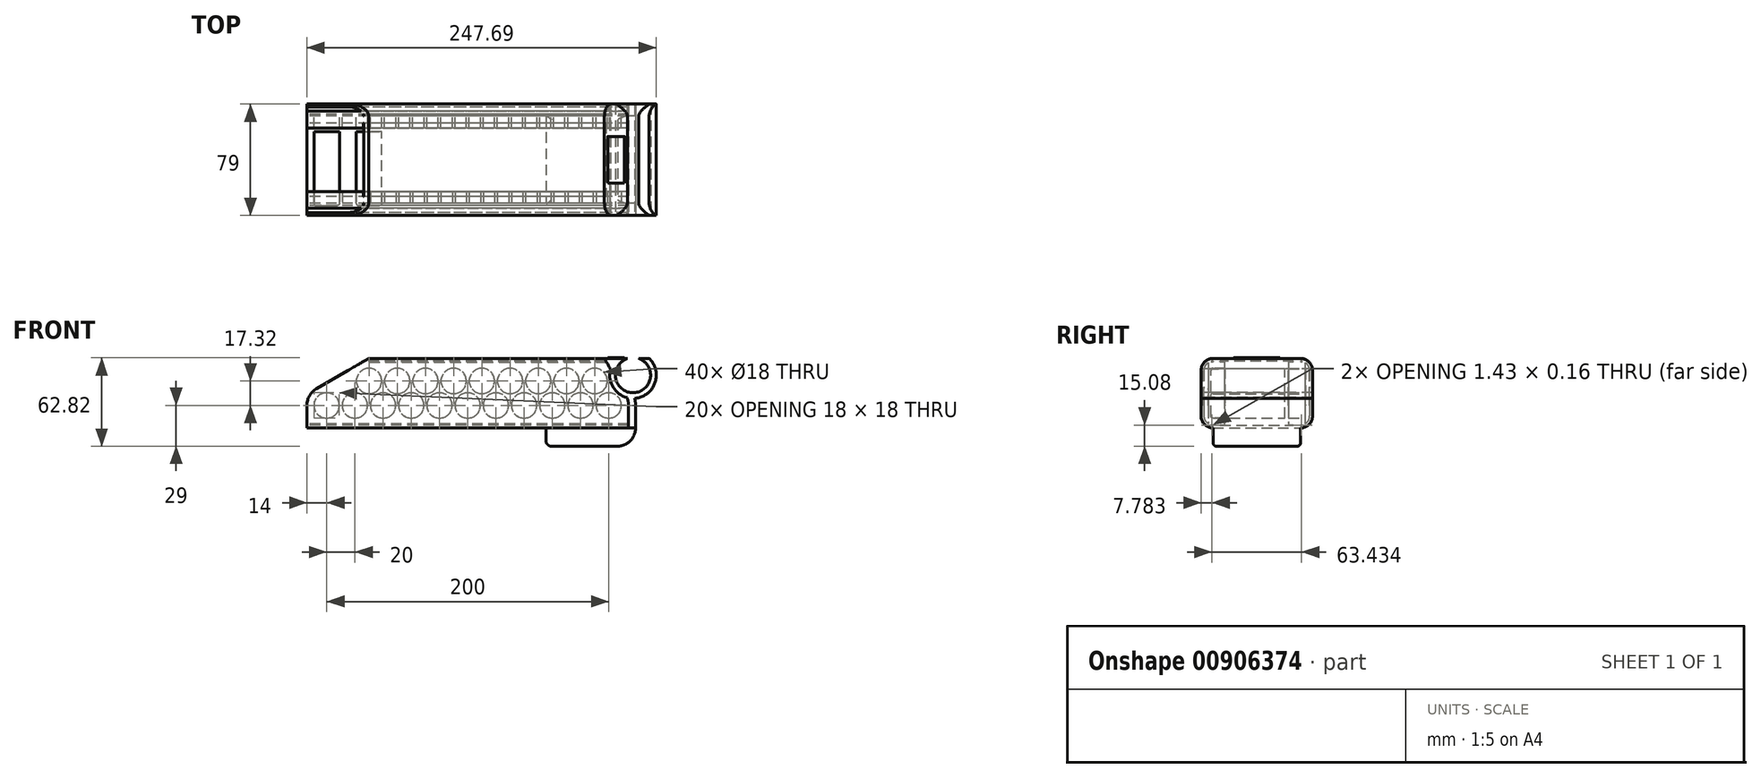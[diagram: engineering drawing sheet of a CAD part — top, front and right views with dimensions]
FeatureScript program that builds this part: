
annotation { "Feature Type Name" : "Feature", "Feature Type Description" : "" }
export const myFeature = defineFeature(function(context is Context, id is Id, definition is map)
    precondition{}
    {
        {
            var Q0;
            Q0=qCreatedBy(makeId("Front.planeOp"),FACE);
            var sketch = newSketch(context, id + "F0", { "sketchPlane" : qUnion([Q0])});
            skCircle(sketch, "E0", {"center": v(0, 0) * mm, "radius": 9 * mm});
            skCircle(sketch, "E1.0.1.0", {"center": v(30, 17.32) * mm, "radius": 9 * mm});
            skCircle(sketch, "E1.1.0.0", {"center": v(20, 0) * mm, "radius": 9 * mm});
            skCircle(sketch, "E1.1.1.0", {"center": v(50, 17.32) * mm, "radius": 9 * mm});
            skCircle(sketch, "E1.2.0.0", {"center": v(40, 0) * mm, "radius": 9 * mm});
            skCircle(sketch, "E1.2.1.0", {"center": v(70, 17.32) * mm, "radius": 9 * mm});
            skCircle(sketch, "E1.3.0.0", {"center": v(60, 0) * mm, "radius": 9 * mm});
            skCircle(sketch, "E1.3.1.0", {"center": v(90, 17.32) * mm, "radius": 9 * mm});
            skCircle(sketch, "E1.4.0.0", {"center": v(80, 0) * mm, "radius": 9 * mm});
            skCircle(sketch, "E1.4.1.0", {"center": v(110, 17.32) * mm, "radius": 9 * mm});
            skCircle(sketch, "E1.5.0.0", {"center": v(100, 0) * mm, "radius": 9 * mm});
            skCircle(sketch, "E1.5.1.0", {"center": v(130, 17.32) * mm, "radius": 9 * mm});
            skCircle(sketch, "E1.6.0.0", {"center": v(120, 0) * mm, "radius": 9 * mm});
            skCircle(sketch, "E1.6.1.0", {"center": v(150, 17.32) * mm, "radius": 9 * mm});
            skCircle(sketch, "E1.7.0.0", {"center": v(140, 0) * mm, "radius": 9 * mm});
            skCircle(sketch, "E1.7.1.0", {"center": v(170, 17.32) * mm, "radius": 9 * mm});
            skCircle(sketch, "E1.8.0.0", {"center": v(160, 0) * mm, "radius": 9 * mm});
            skCircle(sketch, "E1.8.1.0", {"center": v(190, 17.32) * mm, "radius": 9 * mm});
            skCircle(sketch, "E1.9.0.0", {"center": v(180, 0) * mm, "radius": 9 * mm});
            skLineSegment(sketch, "E1.direction1", {"start": v(0, 0) * mm, "end": v(20, 0) * mm, "construction": true});
            skLineSegment(sketch, "E1.direction2", {"start": v(0, 0) * mm, "end": v(30, 17.32) * mm, "construction": true});
            skCircle(sketch, "E2.0.10.0", {"center": v(200, 0) * mm, "radius": 9 * mm});
            skCircle(sketch, "E3", {"center": v(217.19, 21.47) * mm, "radius": 16.5 * mm});
            skCircle(sketch, "E4", {"center": v(217.19, 21.47) * mm, "radius": 12.5 * mm});
            skSolve(sketch);
        }
        {
            var Q0;
            Q0=makeQuery(id+"F0.imprint","IMPRINT",FACE,{"disambiguationData":[TD([[makeQuery(id+"F0.imprint","IMPRINT",EDGE,{"derivedFrom":sQuery(id+"F0.wireOp",EDGE,"E0")}),1.0]])]});
            var Q1;
            Q1=makeQuery(id+"F0.imprint","IMPRINT",FACE,{"disambiguationData":[TD([[makeQuery(id+"F0.imprint","IMPRINT",EDGE,{"derivedFrom":sQuery(id+"F0.wireOp",EDGE,"E1.0.1.0")}),1.0]])]});
            extrude(context, id + "F1", {"entities" : qUnion([Q0, Q1]), "depth" : 65 * mm, "offsetDistance" : 25 * mm});
        }
        {
            var Q0;
            Q0=makeQuery(id+"F1.opExtrude","CAP_FACE",FACE,{"disambiguationData":[OSD([sQuery(id+"F0.wireOp",EDGE,"E1.0.1.0")])],"isStart":false});
            var Q1;
            Q1=makeQuery(id+"F1.opExtrude","CAP_FACE",FACE,{"disambiguationData":[OSD([sQuery(id+"F0.wireOp",EDGE,"E0")])],"isStart":false});
            var Q2;
            Q2=makeQuery(id+"F1.opExtrude","CAP_FACE",FACE,{"disambiguationData":[OSD([sQuery(id+"F0.wireOp",EDGE,"E0")])],"isStart":true});
            var Q3;
            Q3=makeQuery(id+"F1.opExtrude","CAP_FACE",FACE,{"disambiguationData":[OSD([sQuery(id+"F0.wireOp",EDGE,"E1.0.1.0")])],"isStart":true});
            fillet(context, id + "F2", {"entities" : qUnion([Q0, Q1, Q2, Q3]), "radius" : 1.5 * mm, "tangentPropagation" : true, "allowEdgeOverflow" : false});
        }
        {
            var Q0;
            Q0=qCreatedBy(makeId("Right.planeOp"),FACE);
            cPlane(context, id + "F3", {"entities" : qUnion([Q0]), "cplaneType" : CPlaneType.OFFSET, "offset" : 50 * mm, "oppositeDirection" : true, "width" : 150 * mm, "height" : 150 * mm});
        }
        {
            var Q0;
            Q0=qCreatedBy(id+"F3.planeOp",FACE);
            var sketch = newSketch(context, id + "F4", { "sketchPlane" : qUnion([Q0])});
            skLineSegment(sketch, "E5", {"start": v(-10, 31.16) * mm, "end": v(-6.5, 31.16) * mm});
            skLineSegment(sketch, "E6", {"start": v(-1.5, 31.16) * mm, "end": v(-1.5, 30.16) * mm});
            skLineSegment(sketch, "E7", {"start": v(-1.5, 30.16) * mm, "end": v(-6.5, 30.16) * mm});
            skLineSegment(sketch, "E8", {"start": v(-6.5, 30.16) * mm, "end": v(-6.5, 31.16) * mm});
            skLineSegment(sketch, "E9.trimOffspring", {"start": v(-1.5, 31.16) * mm, "end": v(2, 31.16) * mm});
            skPoint(sketch, "E10", {"position": v(-1.5, -9) * mm});
            skPoint(sketch, "E11", {"position": v(-1.5, 26.32) * mm});
            skLineSegment(sketch, "E12", {"start": v(-1.5, 26.32) * mm, "end": v(-1.5, -9) * mm, "construction": true});
            skLineSegment(sketch, "E13", {"start": v(-1.5, 8.66) * mm, "end": v(15.76, 8.66) * mm, "construction": true});
            skLineSegment(sketch, "E14", {"start": v(2, 31.16) * mm, "end": v(2, 8.66) * mm});
            skLineSegment(sketch, "E15", {"start": v(-10, 31.16) * mm, "end": v(-10, 8.66) * mm});
            skLineSegment(sketch, "E16.MirrorCS", {"start": v(2, -13.84) * mm, "end": v(2, 8.66) * mm});
            skLineSegment(sketch, "E17.MirrorCS", {"start": v(-1.5, -13.84) * mm, "end": v(2, -13.84) * mm});
            skLineSegment(sketch, "E18.MirrorCS", {"start": v(-1.5, -13.84) * mm, "end": v(-1.5, -12.84) * mm});
            skLineSegment(sketch, "E19.MirrorCS", {"start": v(-1.5, -12.84) * mm, "end": v(-6.5, -12.84) * mm});
            skLineSegment(sketch, "E20.MirrorCS", {"start": v(-10, -13.84) * mm, "end": v(-6.5, -13.84) * mm});
            skLineSegment(sketch, "E21.MirrorCS", {"start": v(-10, -13.84) * mm, "end": v(-10, 8.66) * mm});
            skLineSegment(sketch, "E22.MirrorCS", {"start": v(-6.5, -12.84) * mm, "end": v(-6.5, -13.84) * mm});
            skSolve(sketch);
        }
        {
            var Q0;
            Q0=makeQuery(id+"F4.imprint","IMPRINT",FACE,{"disambiguationData":[TD([[makeQuery(id+"F4.imprint","IMPRINT",EDGE,{"derivedFrom":sQuery(id+"F4.wireOp",EDGE,"E5")}),-1.0]])]});
            extrude(context, id + "F5", {"entities" : qUnion([Q0]), "depth" : 300 * mm, "offsetDistance" : 25 * mm});
        }
        {
            var Q0;
            Q0=makeQuery(id+"F0.imprint","IMPRINT",FACE,{"disambiguationData":[TD([[makeQuery(id+"F0.imprint","IMPRINT",EDGE,{"derivedFrom":sQuery(id+"F0.wireOp",EDGE,"E1.1.0.0")}),1.0]])]});
            var Q1;
            Q1=makeQuery(id+"F0.imprint","IMPRINT",FACE,{"disambiguationData":[TD([[makeQuery(id+"F0.imprint","IMPRINT",EDGE,{"derivedFrom":sQuery(id+"F0.wireOp",EDGE,"E1.2.0.0")}),1.0]])]});
            var Q2;
            Q2=makeQuery(id+"F0.imprint","IMPRINT",FACE,{"disambiguationData":[TD([[makeQuery(id+"F0.imprint","IMPRINT",EDGE,{"derivedFrom":sQuery(id+"F0.wireOp",EDGE,"E0")}),1.0]])]});
            var Q3;
            Q3=makeQuery(id+"F0.imprint","IMPRINT",FACE,{"disambiguationData":[TD([[makeQuery(id+"F0.imprint","IMPRINT",EDGE,{"derivedFrom":sQuery(id+"F0.wireOp",EDGE,"E1.3.0.0")}),1.0]])]});
            var Q4;
            Q4=makeQuery(id+"F0.imprint","IMPRINT",FACE,{"disambiguationData":[TD([[makeQuery(id+"F0.imprint","IMPRINT",EDGE,{"derivedFrom":sQuery(id+"F0.wireOp",EDGE,"E1.0.1.0")}),1.0]])]});
            var Q5;
            Q5=makeQuery(id+"F0.imprint","IMPRINT",FACE,{"disambiguationData":[TD([[makeQuery(id+"F0.imprint","IMPRINT",EDGE,{"derivedFrom":sQuery(id+"F0.wireOp",EDGE,"E1.1.1.0")}),1.0]])]});
            var Q6;
            Q6=makeQuery(id+"F0.imprint","IMPRINT",FACE,{"disambiguationData":[TD([[makeQuery(id+"F0.imprint","IMPRINT",EDGE,{"derivedFrom":sQuery(id+"F0.wireOp",EDGE,"E1.4.0.0")}),1.0]])]});
            var Q7;
            Q7=makeQuery(id+"F0.imprint","IMPRINT",FACE,{"disambiguationData":[TD([[makeQuery(id+"F0.imprint","IMPRINT",EDGE,{"derivedFrom":sQuery(id+"F0.wireOp",EDGE,"E1.2.1.0")}),1.0]])]});
            var Q8;
            Q8=makeQuery(id+"F0.imprint","IMPRINT",FACE,{"disambiguationData":[TD([[makeQuery(id+"F0.imprint","IMPRINT",EDGE,{"derivedFrom":sQuery(id+"F0.wireOp",EDGE,"E1.3.1.0")}),1.0]])]});
            var Q9;
            Q9=makeQuery(id+"F0.imprint","IMPRINT",FACE,{"disambiguationData":[TD([[makeQuery(id+"F0.imprint","IMPRINT",EDGE,{"derivedFrom":sQuery(id+"F0.wireOp",EDGE,"E1.5.0.0")}),1.0]])]});
            var Q10;
            Q10=makeQuery(id+"F0.imprint","IMPRINT",FACE,{"disambiguationData":[TD([[makeQuery(id+"F0.imprint","IMPRINT",EDGE,{"derivedFrom":sQuery(id+"F0.wireOp",EDGE,"E1.6.0.0")}),1.0]])]});
            var Q11;
            Q11=makeQuery(id+"F0.imprint","IMPRINT",FACE,{"disambiguationData":[TD([[makeQuery(id+"F0.imprint","IMPRINT",EDGE,{"derivedFrom":sQuery(id+"F0.wireOp",EDGE,"E1.4.1.0")}),1.0]])]});
            var Q12;
            Q12=makeQuery(id+"F0.imprint","IMPRINT",FACE,{"disambiguationData":[TD([[makeQuery(id+"F0.imprint","IMPRINT",EDGE,{"derivedFrom":sQuery(id+"F0.wireOp",EDGE,"E1.5.1.0")}),1.0]])]});
            var Q13;
            Q13=makeQuery(id+"F0.imprint","IMPRINT",FACE,{"disambiguationData":[TD([[makeQuery(id+"F0.imprint","IMPRINT",EDGE,{"derivedFrom":sQuery(id+"F0.wireOp",EDGE,"E1.7.0.0")}),1.0]])]});
            var Q14;
            Q14=makeQuery(id+"F0.imprint","IMPRINT",FACE,{"disambiguationData":[TD([[makeQuery(id+"F0.imprint","IMPRINT",EDGE,{"derivedFrom":sQuery(id+"F0.wireOp",EDGE,"E1.8.0.0")}),1.0]])]});
            var Q15;
            Q15=makeQuery(id+"F0.imprint","IMPRINT",FACE,{"disambiguationData":[TD([[makeQuery(id+"F0.imprint","IMPRINT",EDGE,{"derivedFrom":sQuery(id+"F0.wireOp",EDGE,"E1.6.1.0")}),1.0]])]});
            var Q16;
            Q16=makeQuery(id+"F0.imprint","IMPRINT",FACE,{"disambiguationData":[TD([[makeQuery(id+"F0.imprint","IMPRINT",EDGE,{"derivedFrom":sQuery(id+"F0.wireOp",EDGE,"E1.9.0.0")}),1.0]])]});
            var Q17;
            Q17=makeQuery(id+"F0.imprint","IMPRINT",FACE,{"disambiguationData":[TD([[makeQuery(id+"F0.imprint","IMPRINT",EDGE,{"derivedFrom":sQuery(id+"F0.wireOp",EDGE,"E1.7.1.0")}),1.0]])]});
            var Q18;
            Q18=makeQuery(id+"F0.imprint","IMPRINT",FACE,{"disambiguationData":[TD([[makeQuery(id+"F0.imprint","IMPRINT",EDGE,{"derivedFrom":sQuery(id+"F0.wireOp",EDGE,"E1.8.1.0")}),1.0]])]});
            var Q19;
            Q19=makeQuery(id+"F0.imprint","IMPRINT",FACE,{"disambiguationData":[TD([[makeQuery(id+"F0.imprint","IMPRINT",EDGE,{"derivedFrom":sQuery(id+"F0.wireOp",EDGE,"E2.0.10.0")}),1.0]])]});
            var Q20;
            Q20=makeQuery(id+"F0.imprint","IMPRINT",FACE,{"disambiguationData":[TD([[makeQuery(id+"F0.imprint","IMPRINT",EDGE,{"derivedFrom":sQuery(id+"F0.wireOp",EDGE,"E3")}),1.0]])]});
            var Q21;
            Q21=makeQuery(id+"F0.imprint","IMPRINT",FACE,{"disambiguationData":[TD([[makeQuery(id+"F0.imprint","IMPRINT",EDGE,{"derivedFrom":sQuery(id+"F0.wireOp",EDGE,"E4")}),1.0]])]});
            extrude(context, id + "F6", {"entities" : qUnion([Q0, Q1, Q2, Q3, Q4, Q5, Q6, Q7, Q8, Q9, Q10, Q11, Q12, Q13, Q14, Q15, Q16, Q17, Q18, Q19, Q20, Q21]), "operationType" : NewBodyOperationType.REMOVE, "endBound" : BoundingType.SYMMETRIC, "depth" : 25 * mm, "offsetDistance" : 25 * mm});
        }
        {
            var Q0;
            Q0=qCreatedBy(id+"F3.planeOp",FACE);
            var sketch = newSketch(context, id + "F7", { "sketchPlane" : qUnion([Q0])});
            skLineSegment(sketch, "E23", {"start": v(-63.5, 26.32) * mm, "end": v(-1.5, 26.32) * mm, "construction": true});
            skLineSegment(sketch, "E24", {"start": v(-32.5, 26.32) * mm, "end": v(-32.5, -11.54) * mm, "construction": true});
            skSolve(sketch);
        }
        {
            var Q0;
            Q0=sQuery(id+"F7.wireOp",EDGE,"E24");
            cPlane(context, id + "F8", {"entities" : qUnion([Q0]), "cplaneType" : CPlaneType.LINE_ANGLE, "offset" : 25 * mm, "angle" : 90 * degree, "oppositeDirection" : true, "width" : 150 * mm, "height" : 150 * mm});
        }
        {
            var Q0;
            Q0=makeQuery(id+"F5.opExtrude","SWEPT_BODY",BODY,{"disambiguationData":[OSD([sQuery(id+"F4.wireOp",EDGE,"E5"),sQuery(id+"F4.wireOp",EDGE,"GOfXxzIh-MKl5-G1SW-encv-l2kD2u1HkRPf"),sQuery(id+"F4.wireOp",EDGE,"sGYx79DI-effi-Y8B0-5mYI-4x9WzQ8cECE0"),sQuery(id+"F4.wireOp",EDGE,"E6"),sQuery(id+"F4.wireOp",EDGE,"E7"),sQuery(id+"F4.wireOp",EDGE,"E8"),sQuery(id+"F4.wireOp",EDGE,"0fff8e5c-98d8-4951-b7fa-ebcbf429b71a0.MirrorCS"),sQuery(id+"F4.wireOp",EDGE,"65c761b0-a97f-46e1-aada-6f9c72a2409e0.MirrorCS"),sQuery(id+"F4.wireOp",EDGE,"bcdb5b7b-b14c-4f07-bf46-ef241487993a0.MirrorCS"),sQuery(id+"F4.wireOp",EDGE,"ed0ec1d9-44e6-4145-b46c-43663aba06680.MirrorCS"),sQuery(id+"F4.wireOp",EDGE,"8e070cfc-182b-4a56-90c9-7eab96a44dfa0.MirrorCS"),sQuery(id+"F4.wireOp",EDGE,"c2e0f179-9004-4e7f-aabe-193be18498250.MirrorCS"),sQuery(id+"F4.wireOp",EDGE,"E9.trimOffspring"),sQuery(id+"F4.wireOp",EDGE,"f0e1f967-a197-4513-83c4-94e6494bc166.trimOffspring")])]});
            var Q1;
            Q1=qCreatedBy(id+"F8.planeOp",FACE);
            mirror(context, id + "F9", {"entities" : qUnion([Q0]), "mirrorPlane" : qUnion([Q1])});
        }
        {
            var Q0;
            Q0=qCreatedBy(id+"F3.planeOp",FACE);
            var sketch = newSketch(context, id + "F10", { "sketchPlane" : qUnion([Q0])});
            skArc(sketch, "E25", {"start": v(0, 24.82) * mm, "mid": v(-0.44, 25.88) * mm, "end": v(-1.5, 26.32) * mm});
            skArc(sketch, "E26", {"start": v(-1.5, -9) * mm, "mid": v(-0.44, -8.56) * mm, "end": v(0, -7.5) * mm});
            skArc(sketch, "E27", {"start": v(-63.5, 26.32) * mm, "mid": v(-64.56, 25.88) * mm, "end": v(-65, 24.82) * mm});
            skArc(sketch, "E28", {"start": v(-65, -7.5) * mm, "mid": v(-64.56, -8.56) * mm, "end": v(-63.5, -9) * mm});
            skLineSegment(sketch, "E29", {"start": v(0, 24.82) * mm, "end": v(0, -7.5) * mm});
            skLineSegment(sketch, "E30", {"start": v(-1.5, 26.32) * mm, "end": v(-63.5, 26.32) * mm});
            skLineSegment(sketch, "E31", {"start": v(-65, 24.82) * mm, "end": v(-65, -7.5) * mm});
            skLineSegment(sketch, "E32", {"start": v(-63.5, -9) * mm, "end": v(-1.5, -9) * mm});
            skLineSegment(sketch, "E33.0", {"start": v(-63.5, -14) * mm, "end": v(-1.5, -14) * mm});
            skArc(sketch, "E33.1", {"start": v(-70, -7.5) * mm, "mid": v(-68.1, -12.1) * mm, "end": v(-63.5, -14) * mm});
            skArc(sketch, "E33.2", {"start": v(-1.5, -14) * mm, "mid": v(3.1, -12.1) * mm, "end": v(5, -7.5) * mm});
            skLineSegment(sketch, "E33.3", {"start": v(-70, 24.82) * mm, "end": v(-70, -7.5) * mm});
            skLineSegment(sketch, "E33.4", {"start": v(5, 24.82) * mm, "end": v(5, -7.5) * mm});
            skArc(sketch, "E33.5", {"start": v(5, 24.82) * mm, "mid": v(3.1, 29.42) * mm, "end": v(-1.5, 31.32) * mm});
            skLineSegment(sketch, "E33.6", {"start": v(-1.5, 31.32) * mm, "end": v(-63.5, 31.32) * mm});
            skArc(sketch, "E33.7", {"start": v(-63.5, 31.32) * mm, "mid": v(-68.1, 29.42) * mm, "end": v(-70, 24.82) * mm});
            skArc(sketch, "E34.0", {"start": v(7, 24.82) * mm, "mid": v(4.51, 30.83) * mm, "end": v(-1.5, 33.32) * mm});
            skLineSegment(sketch, "E34.1", {"start": v(7, 24.82) * mm, "end": v(7, -7.5) * mm});
            skLineSegment(sketch, "E34.2", {"start": v(-1.5, 33.32) * mm, "end": v(-63.5, 33.32) * mm});
            skArc(sketch, "E34.3", {"start": v(-1.5, -16) * mm, "mid": v(4.51, -13.51) * mm, "end": v(7, -7.5) * mm});
            skArc(sketch, "E34.4", {"start": v(-63.5, 33.32) * mm, "mid": v(-69.51, 30.83) * mm, "end": v(-72, 24.82) * mm});
            skLineSegment(sketch, "E34.5", {"start": v(-72, 24.82) * mm, "end": v(-72, -7.5) * mm});
            skArc(sketch, "E34.6", {"start": v(-72, -7.5) * mm, "mid": v(-69.51, -13.51) * mm, "end": v(-63.5, -16) * mm});
            skLineSegment(sketch, "E34.7", {"start": v(-63.5, -16) * mm, "end": v(-1.5, -16) * mm});
            skLineSegment(sketch, "E35.0", {"start": v(-1.5, 31.32) * mm, "end": v(-1.5, 30.16) * mm});
            skLineSegment(sketch, "E36.0", {"start": v(-1.5, 30.16) * mm, "end": v(-6.5, 30.16) * mm});
            skLineSegment(sketch, "E37.0", {"start": v(-6.5, 31.16) * mm, "end": v(-6.5, 31.32) * mm});
            skLineSegment(sketch, "E38.0", {"start": v(-58.5, 30.16) * mm, "end": v(-58.5, 31.32) * mm});
            skLineSegment(sketch, "E39.0", {"start": v(-63.5, 30.16) * mm, "end": v(-58.5, 30.16) * mm});
            skLineSegment(sketch, "E40.0", {"start": v(-63.5, 31.32) * mm, "end": v(-63.5, 30.16) * mm});
            skLineSegment(sketch, "E41.0", {"start": v(-58.5, -12.84) * mm, "end": v(-58.5, -14) * mm});
            skLineSegment(sketch, "E42.0", {"start": v(-63.5, -12.84) * mm, "end": v(-58.5, -12.84) * mm});
            skLineSegment(sketch, "E43.0", {"start": v(-63.5, -14) * mm, "end": v(-63.5, -12.84) * mm});
            skLineSegment(sketch, "E44.0", {"start": v(-1.5, -12.84) * mm, "end": v(-6.5, -12.84) * mm});
            skLineSegment(sketch, "E45.0", {"start": v(-1.5, -14) * mm, "end": v(-1.5, -12.84) * mm});
            skLineSegment(sketch, "E46.0", {"start": v(-6.5, -12.84) * mm, "end": v(-6.5, -14) * mm});
            skPoint(sketch, "E47.orphan", {"position": v(-1.5, -13.84) * mm});
            skPoint(sketch, "E48.orphan", {"position": v(-6.5, -13.84) * mm});
            skPoint(sketch, "E49.orphan", {"position": v(-58.5, -13.84) * mm});
            skPoint(sketch, "E50.orphan", {"position": v(-63.5, -13.84) * mm});
            skPoint(sketch, "E51.orphan", {"position": v(-63.5, 31.16) * mm});
            skPoint(sketch, "E52.orphan", {"position": v(-58.5, 31.16) * mm});
            skPoint(sketch, "E53.orphan", {"position": v(-6.5, 30.16) * mm});
            skPoint(sketch, "E54.orphan", {"position": v(-1.5, 31.16) * mm});
            skLineSegment(sketch, "E55.0", {"start": v(-6.5, 30.16) * mm, "end": v(-6.5, 31.16) * mm});
            skSolve(sketch);
        }
        {
            var Q0;
            Q0=makeQuery(id+"F10.imprint","IMPRINT",FACE,{"disambiguationData":[TD([[makeQuery(id+"F10.imprint","IMPRINT",EDGE,{"derivedFrom":sQuery(id+"F10.wireOp",EDGE,"E33.0")}),-1.0]])]});
            extrude(context, id + "F11", {"entities" : qUnion([Q0]), "operationType" : NewBodyOperationType.REMOVE, "depth" : 400 * mm, "offsetDistance" : 25 * mm});
        }
        {
            var Q0;
            Q0=makeQuery(id+"F10.imprint","IMPRINT",FACE,{"disambiguationData":[TD([[makeQuery(id+"F10.imprint","IMPRINT",EDGE,{"derivedFrom":sQuery(id+"F10.wireOp",EDGE,"E33.0")}),-1.0]])]});
            extrude(context, id + "F12", {"entities" : qUnion([Q0]), "depth" : 300 * mm, "offsetDistance" : 25 * mm});
        }
        {
            var Q0;
            Q0=qCreatedBy(makeId("Front.planeOp"),FACE);
            cPlane(context, id + "F13", {"entities" : qUnion([Q0]), "cplaneType" : CPlaneType.OFFSET, "offset" : 200 * mm, "oppositeDirection" : true, "width" : 150 * mm, "height" : 150 * mm});
        }
        {
            var Q0;
            Q0=qCreatedBy(id+"F13.planeOp",FACE);
            var sketch = newSketch(context, id + "F14", { "sketchPlane" : qUnion([Q0])});
            skCircle(sketch, "E56.0", {"center": v(30, 17.32) * mm, "radius": 9 * mm});
            skLineSegment(sketch, "E57.0", {"start": v(51.88, 46.12) * mm, "end": v(-7, 12.12) * mm});
            skLineSegment(sketch, "E58.0", {"start": v(-55, -12.5) * mm, "end": v(-55, 29.82) * mm});
            skLineSegment(sketch, "E58.3", {"start": v(-55, 29.82) * mm, "end": v(23.65, 29.82) * mm});
            skArc(sketch, "E59.0", {"start": v(-7, 12.12) * mm, "mid": v(-12.12, 7) * mm, "end": v(-14, 0) * mm});
            skLineSegment(sketch, "E60", {"start": v(-14, 0) * mm, "end": v(-14, -25.46) * mm});
            skLineSegment(sketch, "E61", {"start": v(238.69, 49.58) * mm, "end": v(269.05, 49.58) * mm});
            skLineSegment(sketch, "E62", {"start": v(269.05, 49.58) * mm, "end": v(269.05, -36.3) * mm});
            skLineSegment(sketch, "E63", {"start": v(269.05, -36.3) * mm, "end": v(214, -36.3) * mm});
            skLineSegment(sketch, "E64", {"start": v(-14, -25.46) * mm, "end": v(-63.45, -25.46) * mm});
            skLineSegment(sketch, "E65", {"start": v(-63.45, -25.46) * mm, "end": v(-63.45, 49.58) * mm});
            skLineSegment(sketch, "E66", {"start": v(-63.45, 49.58) * mm, "end": v(52.56, 49.58) * mm});
            skLineSegment(sketch, "E67", {"start": v(52.56, 49.58) * mm, "end": v(51.88, 46.12) * mm});
            skArc(sketch, "E68.0", {"start": v(201.27, 25.8) * mm, "mid": v(202.9, 13.22) * mm, "end": v(212.98, 5.51) * mm});
            skLineSegment(sketch, "E69.0", {"start": v(195.36, 36.03) * mm, "end": v(201.27, 25.8) * mm});
            skArc(sketch, "E70.trimOffspring", {"start": v(202.6, 13.76) * mm, "mid": v(202.52, 13.77) * mm, "end": v(202.43, 13.79) * mm});
            skLineSegment(sketch, "E71", {"start": v(238.69, 49.58) * mm, "end": v(196.26, 49.58) * mm});
            skLineSegment(sketch, "E72", {"start": v(196.26, 49.58) * mm, "end": v(195.36, 36.03) * mm});
            skLineSegment(sketch, "E73.trimOffspring", {"start": v(-14, -12.5) * mm, "end": v(-55, -12.5) * mm});
            skLineSegment(sketch, "E74", {"start": v(214, 0) * mm, "end": v(214, -36.3) * mm});
            skArc(sketch, "E75.trimOffspring", {"start": v(214, 0) * mm, "mid": v(213.71, 2.83) * mm, "end": v(212.85, 5.55) * mm});
            skSolve(sketch);
        }
        {
            var Q0;
            {var subQ1=sQuery(id+"F10.wireOp",EDGE,"E35.0");Q0=makeQuery(id+"F10.imprint","IMPRINT",FACE,{"disambiguationData":[TD([[makeQuery(id+"F10.imprint","IMPRINT",EDGE,{"derivedFrom":subQ1}),-1.0]])]});}
            var Q1;
            Q1=makeQuery(id+"F10.imprint","IMPRINT",FACE,{"disambiguationData":[TD([[makeQuery(id+"F10.imprint","IMPRINT",EDGE,{"derivedFrom":sQuery(id+"F10.wireOp",EDGE,"E44.0")}),1.0]])]});
            var Q2;
            {var subQ2=sQuery(id+"F10.wireOp",EDGE,"E41.0");Q2=makeQuery(id+"F10.imprint","IMPRINT",FACE,{"disambiguationData":[TD([[makeQuery(id+"F10.imprint","IMPRINT",EDGE,{"derivedFrom":subQ2}),-1.0]])]});}
            var Q3;
            {var subQ2=sQuery(id+"F10.wireOp",EDGE,"E38.0");Q3=makeQuery(id+"F10.imprint","IMPRINT",FACE,{"disambiguationData":[TD([[makeQuery(id+"F10.imprint","IMPRINT",EDGE,{"derivedFrom":subQ2}),1.0]])]});}
            extrude(context, id + "F15", {"entities" : qUnion([Q0, Q1, Q2, Q3]), "operationType" : NewBodyOperationType.ADD, "depth" : 300 * mm, "offsetDistance" : 25 * mm, "hasSecondDirection" : true, "secondDirectionOppositeDirection" : false, "secondDirectionDepth" : 25 * mm});
        }
        {
            var Q0;
            {var subQ1=sQuery(id+"F14.wireOp",EDGE,"E58.2");Q0=makeQuery(id+"F14.imprint","IMPRINT",FACE,{"disambiguationData":[TD([[makeQuery(id+"F14.imprint","IMPRINT",EDGE,{"derivedFrom":subQ1}),1.0]])]});}
            var Q1;
            {var subQ4=sQuery(id+"F14.wireOp",EDGE,"4b1b3b87-2225-404d-8d70-db46605fedfe.0");Q1=makeQuery(id+"F14.imprint","IMPRINT",FACE,{"disambiguationData":[TD([[makeQuery(id+"F14.imprint","IMPRINT",EDGE,{"derivedFrom":subQ4}),-1.0]])]});}
            var Q2;
            {var subQ1=sQuery(id+"F14.wireOp",EDGE,"E58.0");Q2=makeQuery(id+"F14.imprint","IMPRINT",FACE,{"disambiguationData":[TD([[makeQuery(id+"F14.imprint","IMPRINT",EDGE,{"derivedFrom":subQ1}),-1.0]])]});}
            var Q3;
            {var subQ1=sQuery(id+"F14.wireOp",EDGE,"E58.0");Q3=makeQuery(id+"F14.imprint","IMPRINT",FACE,{"disambiguationData":[TD([[makeQuery(id+"F14.imprint","IMPRINT",EDGE,{"derivedFrom":subQ1}),1.0]])]});}
            var Q4;
            {var subQ0=sQuery(id+"F14.wireOp",EDGE,"E68.0");var subQ1=sQuery(id+"F14.wireOp",EDGE,"E58.3");var subQ2=makeQuery(id+"F14.imprint","INTERSECT",VERTEX,{"disambiguationData":[OD(0.0)],"derivedFrom":[subQ1,subQ0]});Q4=makeQuery(id+"F14.imprint","IMPRINT",FACE,{"disambiguationData":[TD([[makeQuery(id+"F14.imprint","IMPRINT",EDGE,{"disambiguationData":[TD([[subQ2,-1.0]])],"derivedFrom":subQ1}),-1.0]])]});}
            var Q5;
            {var subQ0=sQuery(id+"F14.wireOp",EDGE,"E68.0");var subQ1=sQuery(id+"F14.wireOp",EDGE,"E58.3");var subQ2=makeQuery(id+"F14.imprint","INTERSECT",VERTEX,{"disambiguationData":[OD(0.0)],"derivedFrom":[subQ1,subQ0]});Q5=makeQuery(id+"F14.imprint","IMPRINT",FACE,{"disambiguationData":[TD([[makeQuery(id+"F14.imprint","IMPRINT",EDGE,{"disambiguationData":[TD([[subQ2,-1.0]])],"derivedFrom":subQ1}),1.0]])]});}
            var Q6;
            Q6=makeQuery(id+"F14.imprint","IMPRINT",FACE,{"disambiguationData":[TD([[makeQuery(id+"F14.imprint","IMPRINT",EDGE,{"derivedFrom":sQuery(id+"F14.wireOp",EDGE,"E61")}),-1.0]])]});
            extrude(context, id + "F16", {"entities" : qUnion([Q0, Q1, Q2, Q3, Q4, Q5, Q6]), "operationType" : NewBodyOperationType.REMOVE, "depth" : 300 * mm, "offsetDistance" : 25 * mm});
        }
        {
            var Q0;
            Q0=makeQuery(id+"F12.opExtrude","SWEPT_FACE",FACE,{"disambiguationData":[OSD([sQuery(id+"F10.wireOp",EDGE,"E34.5")])]});
            var sketch = newSketch(context, id + "F17", { "sketchPlane" : qUnion([Q0])});
            skLineSegment(sketch, "E76.0", {"start": v(201.68, -16) * mm, "end": v(155.46, -16) * mm});
            skArc(sketch, "E77.0", {"start": v(218.33, 5) * mm, "mid": v(232.26, 28.19) * mm, "end": v(205.7, 33.32) * mm});
            skCircle(sketch, "E78.0", {"center": v(217.19, 21.47) * mm, "radius": 12.5 * mm});
            skPoint(sketch, "E79.orphan", {"position": v(-14, -16) * mm});
            skPoint(sketch, "E80.0.start.orphan", {"position": v(185.81, -21) * mm});
            skLineSegment(sketch, "E81.0", {"start": v(205.46, -29) * mm, "end": v(159.46, -29) * mm});
            skLineSegment(sketch, "E82", {"start": v(155.46, -25) * mm, "end": v(155.46, -16) * mm});
            skPoint(sketch, "E83.orphan", {"position": v(-7, 12.12) * mm});
            skArc(sketch, "E84.0", {"start": v(219, 0) * mm, "mid": v(218.83, 2.53) * mm, "end": v(218.33, 5) * mm});
            skLineSegment(sketch, "E84.1", {"start": v(219, 0) * mm, "end": v(219, -7.5) * mm});
            skLineSegment(sketch, "E84.2", {"start": v(219, -7.5) * mm, "end": v(219, -15.97) * mm});
            skLineSegment(sketch, "E85.0", {"start": v(214, 0) * mm, "end": v(214, -7.5) * mm});
            skArc(sketch, "E86.0", {"start": v(214, 0) * mm, "mid": v(213.71, 2.83) * mm, "end": v(212.85, 5.55) * mm});
            skLineSegment(sketch, "E87.0", {"start": v(214, -7.5) * mm, "end": v(214, -16) * mm});
            skArc(sketch, "E88.0", {"start": v(201.27, 25.8) * mm, "mid": v(204.43, 11) * mm, "end": v(218.33, 5) * mm});
            skPoint(sketch, "E89.0.end.orphan", {"position": v(15, 24.82) * mm});
            skArc(sketch, "E90.trimOffspring", {"start": v(218.33, 5) * mm, "mid": v(229.94, 31.93) * mm, "end": v(201.27, 25.8) * mm});
            skArc(sketch, "E91", {"start": v(205.46, -29) * mm, "mid": v(215, -25.37) * mm, "end": v(219, -15.97) * mm});
            skPoint(sketch, "E92.visualSharp", {"position": v(155.46, -29) * mm});
            skArc(sketch, "E92.filletArc", {"start": v(155.46, -25) * mm, "mid": v(156.63, -27.83) * mm, "end": v(159.46, -29) * mm});
            skPoint(sketch, "E93.visualSharp", {"position": v(185.81, 38.32) * mm});
            skPoint(sketch, "E94.orphan", {"position": v(196.93, 33.32) * mm});
            skPoint(sketch, "E95.0.end.orphan", {"position": v(29.71, 33.32) * mm});
            skPoint(sketch, "E96.end.orphan", {"position": v(185.81, 33.32) * mm});
            skLineSegment(sketch, "E97.0", {"start": v(196.93, 33.32) * mm, "end": v(201.27, 25.8) * mm});
            skLineSegment(sketch, "E98", {"start": v(196.93, 33.32) * mm, "end": v(205.7, 33.32) * mm});
            skLineSegment(sketch, "E99", {"start": v(214, -16) * mm, "end": v(201.68, -16) * mm});
            skSolve(sketch);
        }
        {
            var Q0;
            Q0=qCreatedBy(id+"F3.planeOp",FACE);
            var sketch = newSketch(context, id + "F18", { "sketchPlane" : qUnion([Q0])});
            skArc(sketch, "E100.0", {"start": v(30.3, 24.82) * mm, "mid": v(20.99, 47.3) * mm, "end": v(-1.5, 56.62) * mm});
            skLineSegment(sketch, "E100.1", {"start": v(-95.3, 0) * mm, "end": v(-95.3, -7.5) * mm});
            skLineSegment(sketch, "E100.2", {"start": v(-95.3, 12.12) * mm, "end": v(-95.3, 0) * mm});
            skLineSegment(sketch, "E100.3", {"start": v(-95.3, 24.82) * mm, "end": v(-95.3, 12.12) * mm});
            skArc(sketch, "E100.4", {"start": v(-63.5, 56.62) * mm, "mid": v(-85.99, 47.3) * mm, "end": v(-95.3, 24.82) * mm});
            skArc(sketch, "E100.5", {"start": v(-95.3, -7.5) * mm, "mid": v(-85.99, -29.99) * mm, "end": v(-63.5, -39.3) * mm});
            skLineSegment(sketch, "E100.6", {"start": v(-1.5, 56.62) * mm, "end": v(-63.5, 56.62) * mm});
            skLineSegment(sketch, "E100.7", {"start": v(-63.5, -39.3) * mm, "end": v(-1.5, -39.3) * mm});
            skArc(sketch, "E100.8", {"start": v(-1.5, -39.3) * mm, "mid": v(20.99, -29.99) * mm, "end": v(30.3, -7.5) * mm});
            skLineSegment(sketch, "E100.9", {"start": v(30.3, 0) * mm, "end": v(30.3, -7.5) * mm});
            skLineSegment(sketch, "E100.10", {"start": v(30.3, 12.12) * mm, "end": v(30.3, 0) * mm});
            skLineSegment(sketch, "E100.11", {"start": v(30.3, 24.82) * mm, "end": v(30.3, 12.12) * mm});
            skArc(sketch, "E101.0", {"start": v(7, 24.82) * mm, "mid": v(4.51, 30.83) * mm, "end": v(-1.5, 33.32) * mm});
            skLineSegment(sketch, "E102.0", {"start": v(7, 24.82) * mm, "end": v(7, 12.12) * mm});
            skLineSegment(sketch, "E103.0", {"start": v(7, 12.12) * mm, "end": v(7, 0) * mm});
            skLineSegment(sketch, "E104.0", {"start": v(7, 0) * mm, "end": v(7, -7.5) * mm});
            skArc(sketch, "E105.0", {"start": v(-1.5, -16) * mm, "mid": v(4.51, -13.51) * mm, "end": v(7, -7.5) * mm});
            skArc(sketch, "E106.0", {"start": v(-72, -7.5) * mm, "mid": v(-69.51, -13.51) * mm, "end": v(-63.5, -16) * mm});
            skLineSegment(sketch, "E107.0", {"start": v(-72, 0) * mm, "end": v(-72, -7.5) * mm});
            skLineSegment(sketch, "E108.0", {"start": v(-72, 12.12) * mm, "end": v(-72, 0) * mm});
            skArc(sketch, "E109.0", {"start": v(-63.5, 33.32) * mm, "mid": v(-69.51, 30.83) * mm, "end": v(-72, 24.82) * mm});
            skLineSegment(sketch, "E110.0", {"start": v(-72, 24.82) * mm, "end": v(-72, 12.12) * mm});
            skPoint(sketch, "E111.orphan", {"position": v(7, 38.32) * mm});
            skPoint(sketch, "E112.orphan", {"position": v(-72, 38.32) * mm});
            skPoint(sketch, "E113.visualSharp", {"position": v(-1.5, 38.32) * mm});
            skPoint(sketch, "E114.visualSharp", {"position": v(-63.5, 38.32) * mm});
            skLineSegment(sketch, "E115.0", {"start": v(-4, -29) * mm, "end": v(-61, -29) * mm});
            skLineSegment(sketch, "E116", {"start": v(-1.5, -16) * mm, "end": v(-1.5, -26.5) * mm});
            skLineSegment(sketch, "E117", {"start": v(-63.5, -16) * mm, "end": v(-63.5, -26.5) * mm});
            skPoint(sketch, "E118.orphan", {"position": v(7, -29) * mm});
            skPoint(sketch, "E119.orphan", {"position": v(-72, -29) * mm});
            skPoint(sketch, "E120.visualSharp", {"position": v(-1.5, -29) * mm});
            skArc(sketch, "E120.filletArc", {"start": v(-4, -29) * mm, "mid": v(-2.23, -28.27) * mm, "end": v(-1.5, -26.5) * mm});
            skPoint(sketch, "E121.visualSharp", {"position": v(-63.5, -29) * mm});
            skArc(sketch, "E121.filletArc", {"start": v(-63.5, -26.5) * mm, "mid": v(-62.77, -28.27) * mm, "end": v(-61, -29) * mm});
            skLineSegment(sketch, "E122", {"start": v(-1.5, 33.32) * mm, "end": v(-63.5, 33.32) * mm});
            skSolve(sketch);
        }
        {
            var Q0;
            Q0=makeQuery(id+"F17.imprint","IMPRINT",FACE,{"disambiguationData":[TD([[makeQuery(id+"F17.imprint","IMPRINT",EDGE,{"derivedFrom":sQuery(id+"F17.wireOp",EDGE,"E76.0")}),1.0]])]});
            var Q1;
            {var subQ0=sQuery(id+"F17.wireOp",EDGE,"E97.0");Q1=makeQuery(id+"F17.imprint","IMPRINT",FACE,{"disambiguationData":[TD([[makeQuery(id+"F17.imprint","IMPRINT",EDGE,{"derivedFrom":subQ0}),1.0]])]});}
            var Q2;
            Q2=makeQuery(id+"F17.imprint","IMPRINT",FACE,{"disambiguationData":[TD([[makeQuery(id+"F17.imprint","IMPRINT",EDGE,{"derivedFrom":sQuery(id+"F17.wireOp",EDGE,"E78.0")}),-1.0]])]});
            extrude(context, id + "F19", {"entities" : qUnion([Q0, Q1, Q2]), "oppositeDirection" : true, "depth" : 79 * mm, "offsetDistance" : 25 * mm});
        }
        {
            var Q0;
            Q0=makeQuery(id+"F18.imprint","IMPRINT",FACE,{"disambiguationData":[TD([[makeQuery(id+"F18.imprint","IMPRINT",EDGE,{"derivedFrom":sQuery(id+"F18.wireOp",EDGE,"E100.0")}),1.0]])]});
            var Q1;
            Q1=makeQuery(id+"F18.imprint","IMPRINT",FACE,{"disambiguationData":[TD([[makeQuery(id+"F18.imprint","IMPRINT",EDGE,{"derivedFrom":sQuery(id+"F18.wireOp",EDGE,"6d19e27c-c4e0-4d71-8ca3-83cf312b21e4.0")}),1.0]])]});
            extrude(context, id + "F20", {"entities" : qUnion([Q0, Q1]), "operationType" : NewBodyOperationType.REMOVE, "depth" : 300 * mm, "offsetDistance" : 25 * mm});
        }
        {
            var Q0;
            Q0=makeQuery(id+"F20.boolean.opBoolean","MERGE",FACE,{"derivedFrom":[makeQuery(id+"F19.opExtrude","SWEPT_FACE",FACE,{"disambiguationData":[OSD([sQuery(id+"F17.wireOp",EDGE,"E98")])]})],"fromTools":[makeQuery(id+"F20.opExtrude","SWEPT_FACE",FACE,{"disambiguationData":[OSD([sQuery(id+"F18.wireOp",EDGE,"E122")])]})]});
            var sketch = newSketch(context, id + "F21", { "sketchPlane" : qUnion([Q0])});
            skLineSegment(sketch, "E123.bottom", {"start": v(199.21, -16) * mm, "end": v(211.21, -16) * mm});
            skLineSegment(sketch, "E124", {"start": v(213.21, -32.5) * mm, "end": v(190.7, -32.5) * mm, "construction": true});
            skLineSegment(sketch, "E125", {"start": v(199.21, -16) * mm, "end": v(199.21, -32.5) * mm});
            skLineSegment(sketch, "E126", {"start": v(211.21, -16) * mm, "end": v(211.21, -32.5) * mm});
            skLineSegment(sketch, "E127.MirrorCS", {"start": v(199.21, -49) * mm, "end": v(199.21, -32.5) * mm});
            skLineSegment(sketch, "E128.MirrorCS", {"start": v(199.21, -49) * mm, "end": v(211.21, -49) * mm});
            skLineSegment(sketch, "E129.MirrorCS", {"start": v(211.21, -49) * mm, "end": v(211.21, -32.5) * mm});
            skSolve(sketch);
        }
        {
            var Q0;
            Q0=makeQuery(id+"F21.imprint","IMPRINT",FACE,{"disambiguationData":[TD([[makeQuery(id+"F21.imprint","IMPRINT",EDGE,{"derivedFrom":sQuery(id+"F21.wireOp",EDGE,"E123.bottom")}),-1.0]])]});
            extrude(context, id + "F22", {"entities" : qUnion([Q0]), "depth" : 0.5 * mm, "offsetDistance" : 25 * mm});
        }
        {
            var Q0;
            Q0=makeQuery(id+"F22.opExtrude","CAP_FACE",FACE,{"disambiguationData":[OSD([sQuery(id+"F21.wireOp",EDGE,"E123.bottom"),sQuery(id+"F21.wireOp",EDGE,"E125"),sQuery(id+"F21.wireOp",EDGE,"E126"),sQuery(id+"F21.wireOp",EDGE,"E127.MirrorCS"),sQuery(id+"F21.wireOp",EDGE,"E128.MirrorCS"),sQuery(id+"F21.wireOp",EDGE,"E129.MirrorCS")])],"isStart":false});
            fillet(context, id + "F23", {"entities" : qUnion([Q0]), "radius" : 0.5 * mm, "tangentPropagation" : true, "allowEdgeOverflow" : false});
        }
    });
